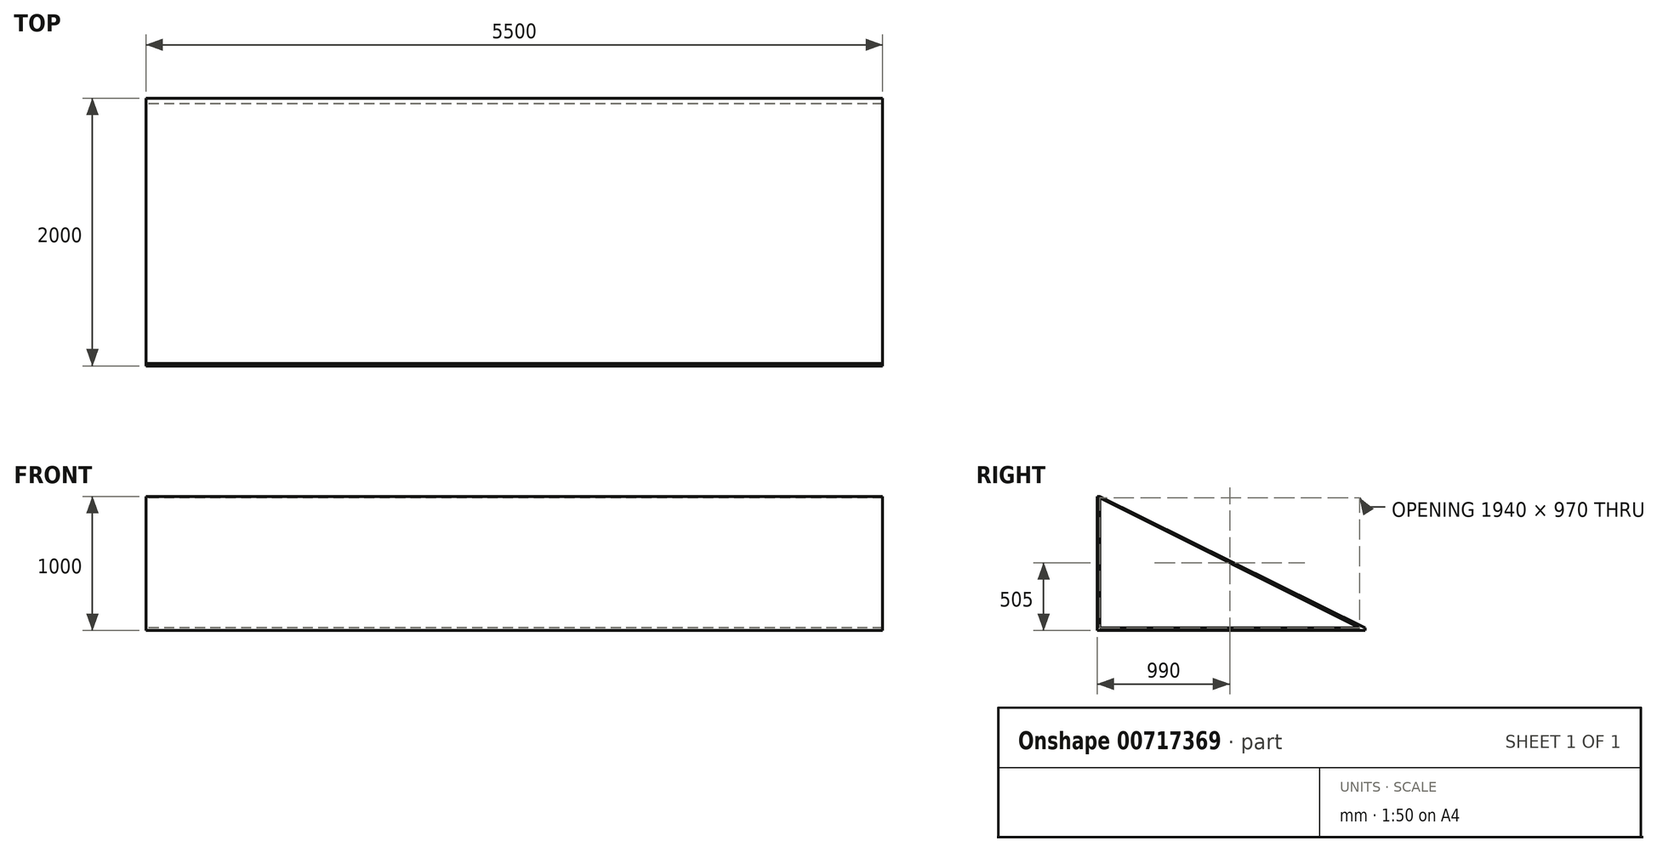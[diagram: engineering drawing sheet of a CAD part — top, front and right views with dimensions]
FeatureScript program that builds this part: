
annotation { "Feature Type Name" : "Feature", "Feature Type Description" : "" }
export const myFeature = defineFeature(function(context is Context, id is Id, definition is map)
    precondition{}
    {
        {
            var Q0;
            Q0=qCreatedBy(makeId("Right.planeOp"),FACE);
            var sketch = newSketch(context, id + "F0", { "sketchPlane" : qUnion([Q0])});
            skLineSegment(sketch, "E0.bottom", {"start": v(0, 0) * mm, "end": v(20, 0) * mm});
            skLineSegment(sketch, "E0.top", {"start": v(0, 1000) * mm, "end": v(20, 1000) * mm});
            skLineSegment(sketch, "E0.left", {"start": v(0, 0) * mm, "end": v(0, 1000) * mm});
            skLineSegment(sketch, "E0.right", {"start": v(20, 20) * mm, "end": v(20, 990) * mm});
            skLineSegment(sketch, "E1.bottom", {"start": v(0, 0) * mm, "end": v(2000, 0) * mm});
            skLineSegment(sketch, "E1.top", {"start": v(20, 20) * mm, "end": v(1960, 20) * mm});
            skLineSegment(sketch, "E1.left", {"start": v(0, 0) * mm, "end": v(0, 20) * mm});
            skLineSegment(sketch, "E1.right", {"start": v(2000, 0) * mm, "end": v(2000, 20) * mm});
            skLineSegment(sketch, "E2", {"start": v(20, 1000) * mm, "end": v(2000, 20) * mm});
            skLineSegment(sketch, "E3", {"start": v(20, 990) * mm, "end": v(1960, 20) * mm});
            skSolve(sketch);
        }
        {
            var Q0;
            Q0 = qSketchRegion(id + "F0", true);
            extrude(context, id + "F1", {"entities" : qUnion([Q0]), "depth" : 5500 * mm, "offsetDistance" : 25 * mm});
        }
    });
